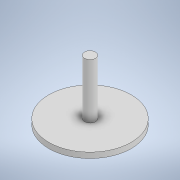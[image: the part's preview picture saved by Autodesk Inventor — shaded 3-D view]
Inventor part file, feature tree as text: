
AUTODESK INVENTOR PART (.ipt)
format: ipt  version: 2021 (Build 250183000, 183)  size: 104,960 bytes
history: native  units: in
note: dims shown in document units (in); Inventor stores cm internally (conversion verified against a paired STEP export)
features: extrude x2, sketch x2
ambient origin geometry x8: Origin, YZ Plane, XZ Plane, XY Plane, X Axis, Y Axis, Z Axis, Center Point
bodies: Solid1 (feature_tree)
feature tree (4):
  extrude  "Extrusion1"  Depth=2.0in
  extrude  "Extrusion2"  Depth=10.0in TaperAngle=0.0deg
  sketch  "Sketch1"  dims[d0=15.0in d1=2.0in]
  sketch  "Sketch2"  dims[d2=1.0in d3=0.0in d4=10.0in d5=0.0in d6=1.0in d7=0.0in]
